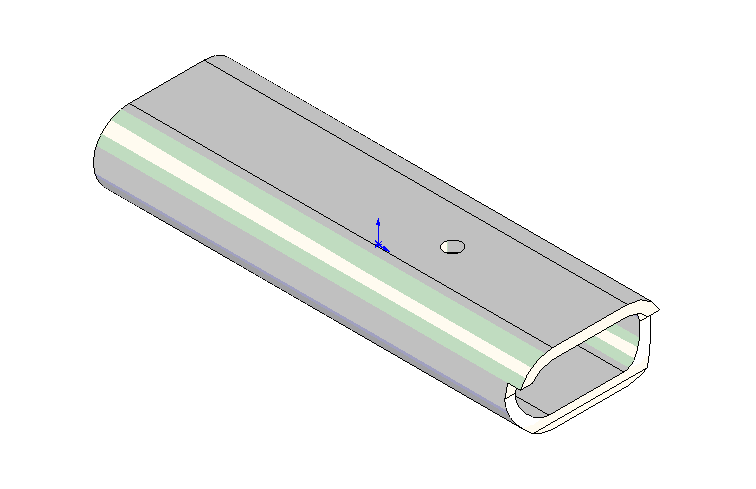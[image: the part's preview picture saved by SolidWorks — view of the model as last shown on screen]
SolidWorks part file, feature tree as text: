
SOLIDWORKS PART (.sldprt)
format: sldprt  version: not decoded by parser v0  size: 242,688 bytes
history: native  units: mm
features: sketch x4, plane x3, cut_extrude x3, material x1, extrude x1 (+10 scaffold rows collapsed)
feature tree (22):
  scaffold x10  (default folders/planes/origin — collapsed)
  material  "Matériau <non spécifié>"
  plane  "Plan de face"
  plane  "Plan de dessus"
  plane  "Plan de droite"
  sketch  "Esquisse1"  dims[c1.D2=8.5mm c1.D1=17.0mm c2.D2=35.0mm c2.D3=2.5mm]
  extrude  "Extrusion1"  Depth=102mm
  sketch  "Esquisse3"  dims[D3=11.0mm D1=5.0mm D2=3.0mm D4=3.0mm]
  cut_extrude  "Enlèv. mat.-Extru.2"  [1 undecoded]
  sketch  "Esquisse4"  dims[D1=4.2mm D2=30.0mm]
  cut_extrude  "Enlèv. mat.-Extru.3"  [1 undecoded]
  sketch  "Esquisse5"  dims[c1.D1=82.0mm c1.D3=82.0mm c2.D1=82.0mm c2.D2=9.5mm c2.D3=44.0mm c3.D2=9.5mm c3.D3=44.0mm]
  cut_extrude  "Enlèv. mat.-Extru.4"  [1 undecoded]
decode coverage: 5 of 8 modeling features carry decoded parameters
note: 3 parameter values undecoded
summary: no parameter record found for 3 features
note: suppression state not decoded; provenance and decode notes live in map.json
